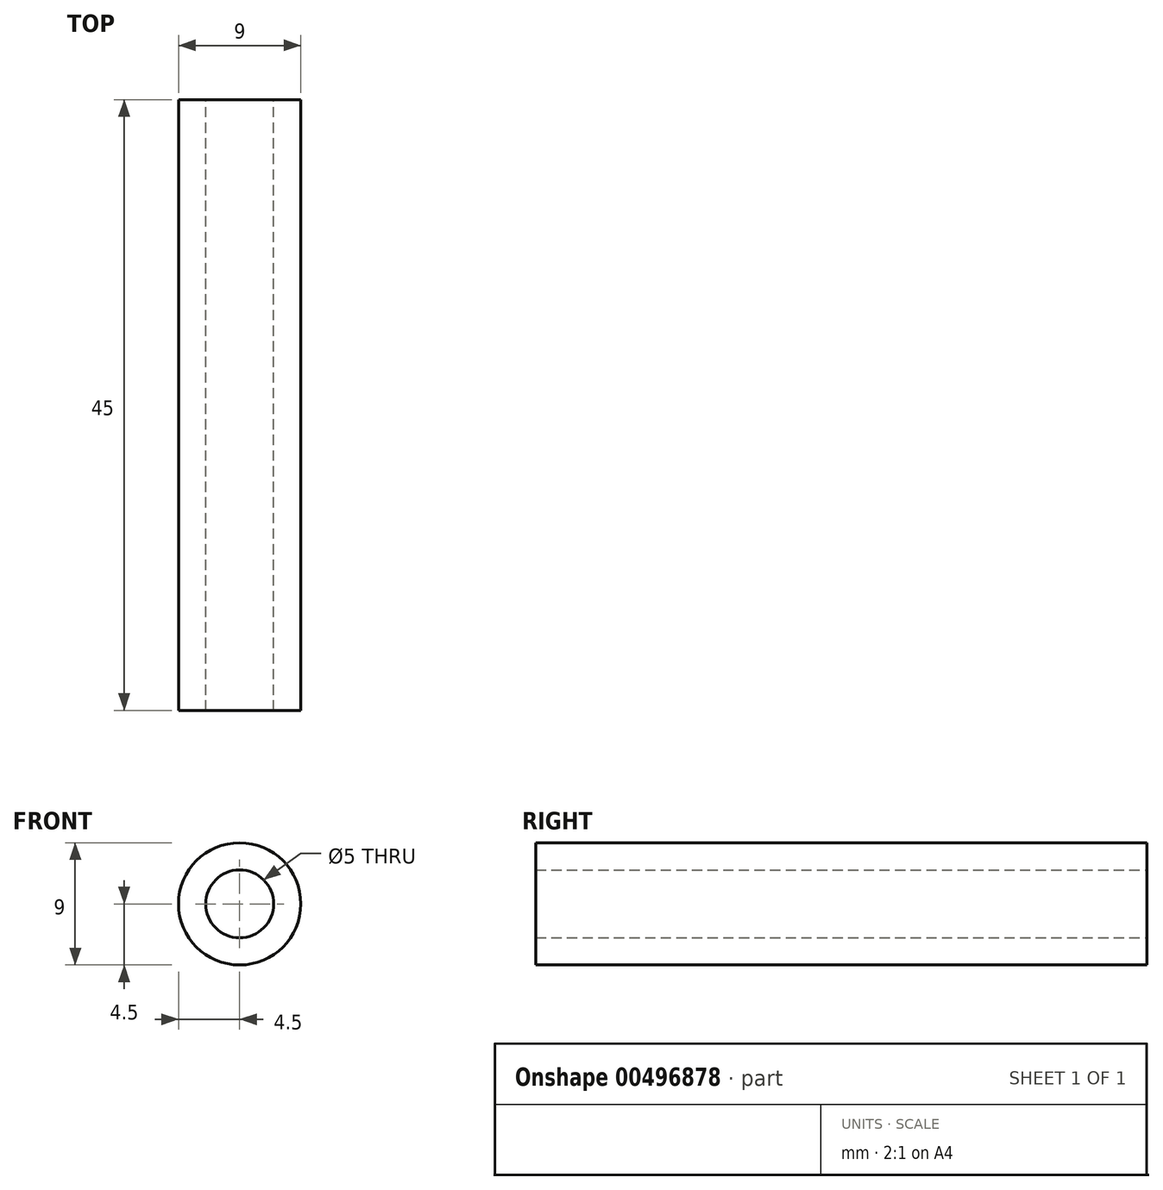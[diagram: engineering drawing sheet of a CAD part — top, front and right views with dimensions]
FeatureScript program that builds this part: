
annotation { "Feature Type Name" : "Feature", "Feature Type Description" : "" }
export const myFeature = defineFeature(function(context is Context, id is Id, definition is map)
    precondition{}
    {
        {
            var Q0;
            Q0=qCreatedBy(makeId("Front.planeOp"),FACE);
            var sketch = newSketch(context, id + "F0", { "sketchPlane" : qUnion([Q0])});
            skCircle(sketch, "E0", {"center": v(0, 0) * mm, "radius": 4.5 * mm});
            skCircle(sketch, "E1", {"center": v(0, 0) * mm, "radius": 2.5 * mm});
            skSolve(sketch);
        }
        {
            var Q0;
            Q0=makeQuery(id+"F0.imprint","IMPRINT",FACE,{"disambiguationData":[TD([[makeQuery(id+"F0.imprint","IMPRINT",EDGE,{"derivedFrom":sQuery(id+"F0.wireOp",EDGE,"E0")}),1.0]])]});
            extrude(context, id + "F1", {"entities" : qUnion([Q0]), "depth" : 45 * mm});
        }
    });
